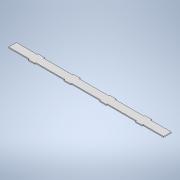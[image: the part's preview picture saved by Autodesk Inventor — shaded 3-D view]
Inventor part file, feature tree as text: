
AUTODESK INVENTOR PART (.ipt)
format: ipt  version: 2022 (Build 260153000, 153)  size: 142,336 bytes
history: native  units: in
note: dims shown in document units (in); Inventor stores cm internally (conversion verified against a paired STEP export)
features: extrude x1, sketch x1
ambient origin geometry x8: Origin, YZ Plane, XZ Plane, XY Plane, X Axis, Y Axis, Z Axis, Center Point
bodies: Solid1 (feature_tree)
feature tree (2):
  extrude  "Extrusion1"  Depth=0.9055in
  sketch  "Sketch1"  dims[d0=18.2677in d1=0.9055in d2=0.1181in d3=0.7874in d4=6.3189in d5=0.1181in d7=1.5748in d9=4.2126in d10=0.3937in d12=0.3937in d14=0.7874in d15=0.1181in d16=0.0in]
